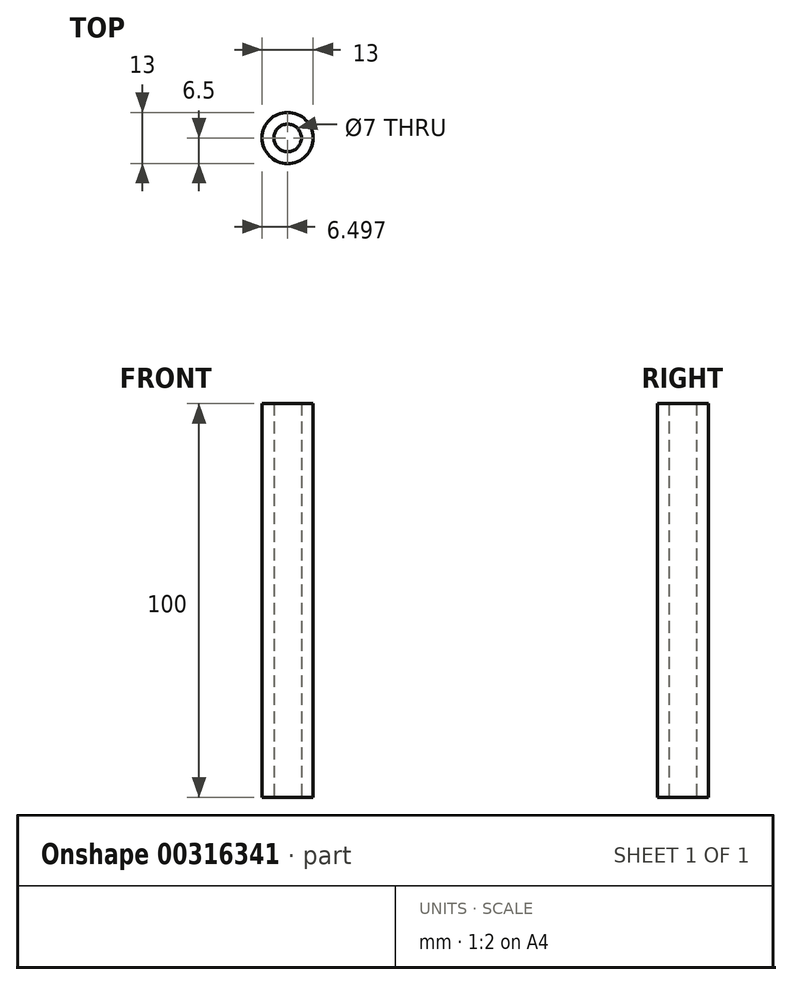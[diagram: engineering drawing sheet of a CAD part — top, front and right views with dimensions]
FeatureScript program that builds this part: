
annotation { "Feature Type Name" : "Feature", "Feature Type Description" : "" }
export const myFeature = defineFeature(function(context is Context, id is Id, definition is map)
    precondition{}
    {
        {
            var Q0;
            Q0=qCreatedBy(makeId("Top.planeOp"),FACE);
            var sketch = newSketch(context, id + "F0", { "sketchPlane" : qUnion([Q0])});
            skSolve(sketch);
        }
        {
            var Q0;
            Q0=qCreatedBy(makeId("Top.planeOp"),FACE);
            var sketch = newSketch(context, id + "F1", { "sketchPlane" : qUnion([Q0])});
            skCircle(sketch, "E0", {"center": v(24.86, 0) * mm, "radius": 6.5 * mm});
            skCircle(sketch, "E1", {"center": v(24.86, 0) * mm, "radius": 3.5 * mm});
            skSolve(sketch);
        }
        {
            var Q0;
            Q0=qSketchRegion(id+"F1",true);
            var Q1;
            Q1=qSketchRegion(id+"F0",true);
            extrude(context, id + "F2", {"entities" : qUnion([Q0, Q1]), "depth" : 100 * mm});
        }
    });
